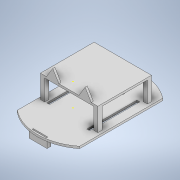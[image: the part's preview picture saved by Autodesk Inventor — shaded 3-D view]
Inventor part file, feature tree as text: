
AUTODESK INVENTOR PART (.ipt)
format: ipt  version: 2021.1 (Build 251245010, 245A)  size: 217,600 bytes
history: native  units: in
note: dims shown in document units (in); Inventor stores cm internally (conversion verified against a paired STEP export)
features: sketch x13, extrude x7, other x1
ambient origin geometry x8: Origin, YZ Plane, XZ Plane, XY Plane, X Axis, Y Axis, Z Axis, Center Point
bodies: Body1 (feature_tree)
feature tree (21):
  other  "솔리드1"
  sketch  "스케치1"
  sketch  "3D 스케치1"
  sketch  "3D 스케치2"
  extrude  "돌출1"  Depth=5.9055in
  extrude  "돌출2"  Depth=7.874in
  extrude  "돌출3"  Depth=0.3937in
  extrude  "돌출4"  Depth=0.3937in
  sketch  "스케치6"
  extrude  "돌출5"  Depth=0.3937in
  sketch  "스케치8"
  sketch  "스케치9"
  extrude  "돌출6"  Depth=0.3937in
  sketch  "스케치11"
  extrude  "돌출8"  Depth=0.3937in
  sketch  "스케치3"
  sketch  "스케치4"
  sketch  "스케치5"
  sketch  "스케치7"
  sketch  "스케치10"
  sketch  "스케치14"
